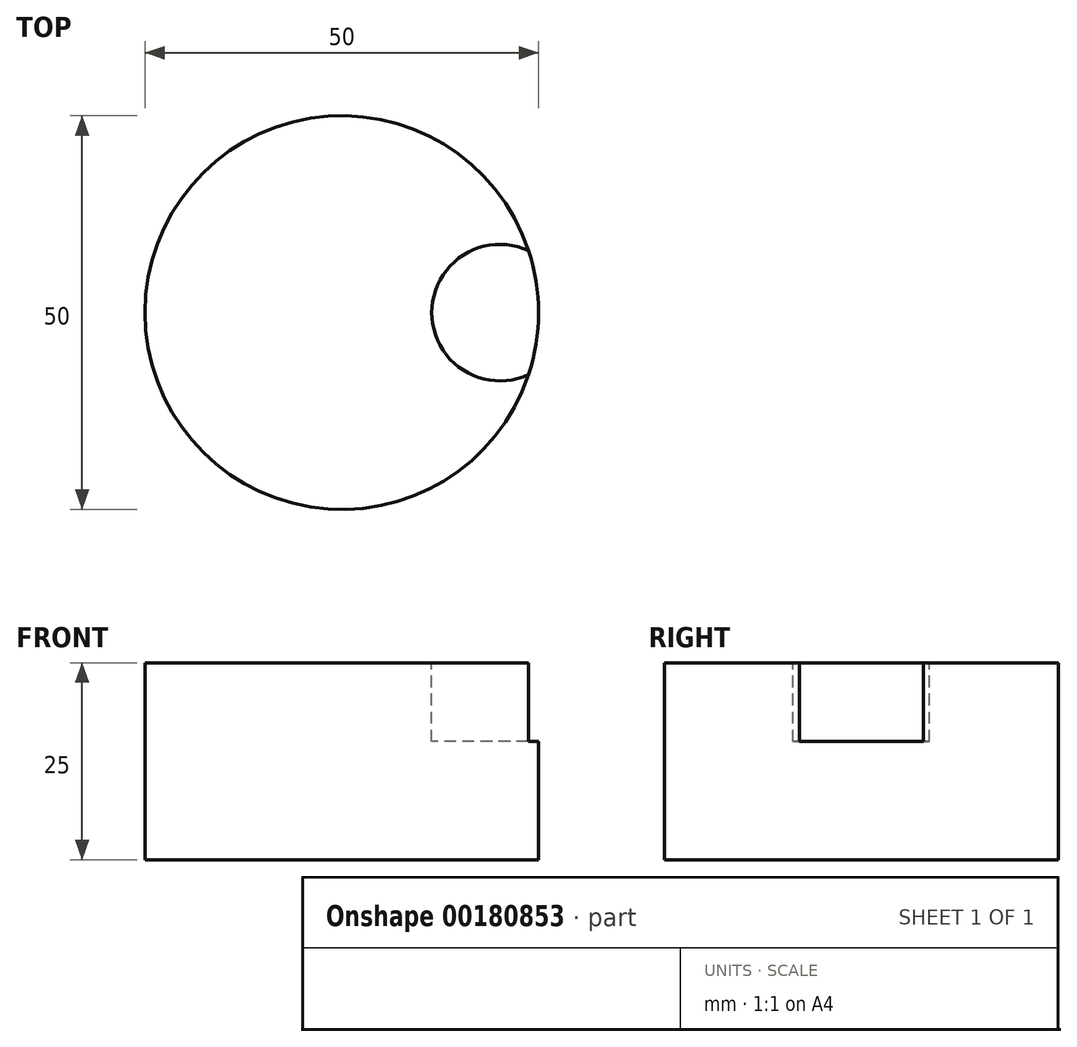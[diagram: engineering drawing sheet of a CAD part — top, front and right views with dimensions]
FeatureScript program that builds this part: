
annotation { "Feature Type Name" : "Feature", "Feature Type Description" : "" }
export const myFeature = defineFeature(function(context is Context, id is Id, definition is map)
    precondition{}
    {
        {
            var Q0;
            Q0=qCreatedBy(makeId("Top.planeOp"),FACE);
            var sketch = newSketch(context, id + "F0", { "sketchPlane" : qUnion([Q0])});
            skCircle(sketch, "E0", {"center": v(0, 0) * mm, "radius": 25 * mm});
            skSolve(sketch);
        }
        {
            var Q0;
            Q0=makeQuery(id+"F0.imprint","IMPRINT",FACE,{"disambiguationData":[TD([[makeQuery(id+"F0.imprint","IMPRINT",EDGE,{"derivedFrom":sQuery(id+"F0.wireOp",EDGE,"E0")}),1.0]])]});
            extrude(context, id + "F1", {"entities" : qUnion([Q0]), "depth" : 25 * mm});
        }
        {
            var Q0;
            Q0=makeQuery(id+"F1.opExtrude","CAP_FACE",FACE,{"disambiguationData":[OSD([sQuery(id+"F0.wireOp",EDGE,"E0")])],"isStart":false});
            var sketch = newSketch(context, id + "F2", { "sketchPlane" : qUnion([Q0])});
            skCircle(sketch, "E1", {"center": v(20.1, 0) * mm, "radius": 8.67 * mm});
            skSolve(sketch);
        }
        {
            var Q0;
            {var subQ0=sQuery(id+"F2.wireOp",EDGE,"E1");var subQ1=makeQuery(id+"F1.opExtrude","CAP_EDGE",EDGE,{"disambiguationData":[OSD([sQuery(id+"F0.wireOp",EDGE,"E0")])],"isStart":false});var subQ2=makeQuery(id+"F2.imprint","INTERSECT",VERTEX,{"disambiguationData":[OD(0.0)],"derivedFrom":[subQ1,subQ0]});Q0=makeQuery(id+"F2.imprint","IMPRINT",FACE,{"disambiguationData":[TD([[makeQuery(id+"F2.imprint","IMPRINT",EDGE,{"disambiguationData":[TD([[subQ2,1.0]])],"derivedFrom":subQ0}),1.0]])]});}
            extrude(context, id + "F3", {"entities" : qUnion([Q0]), "operationType" : NewBodyOperationType.REMOVE, "oppositeDirection" : true, "depth" : 10 * mm});
        }
    });
